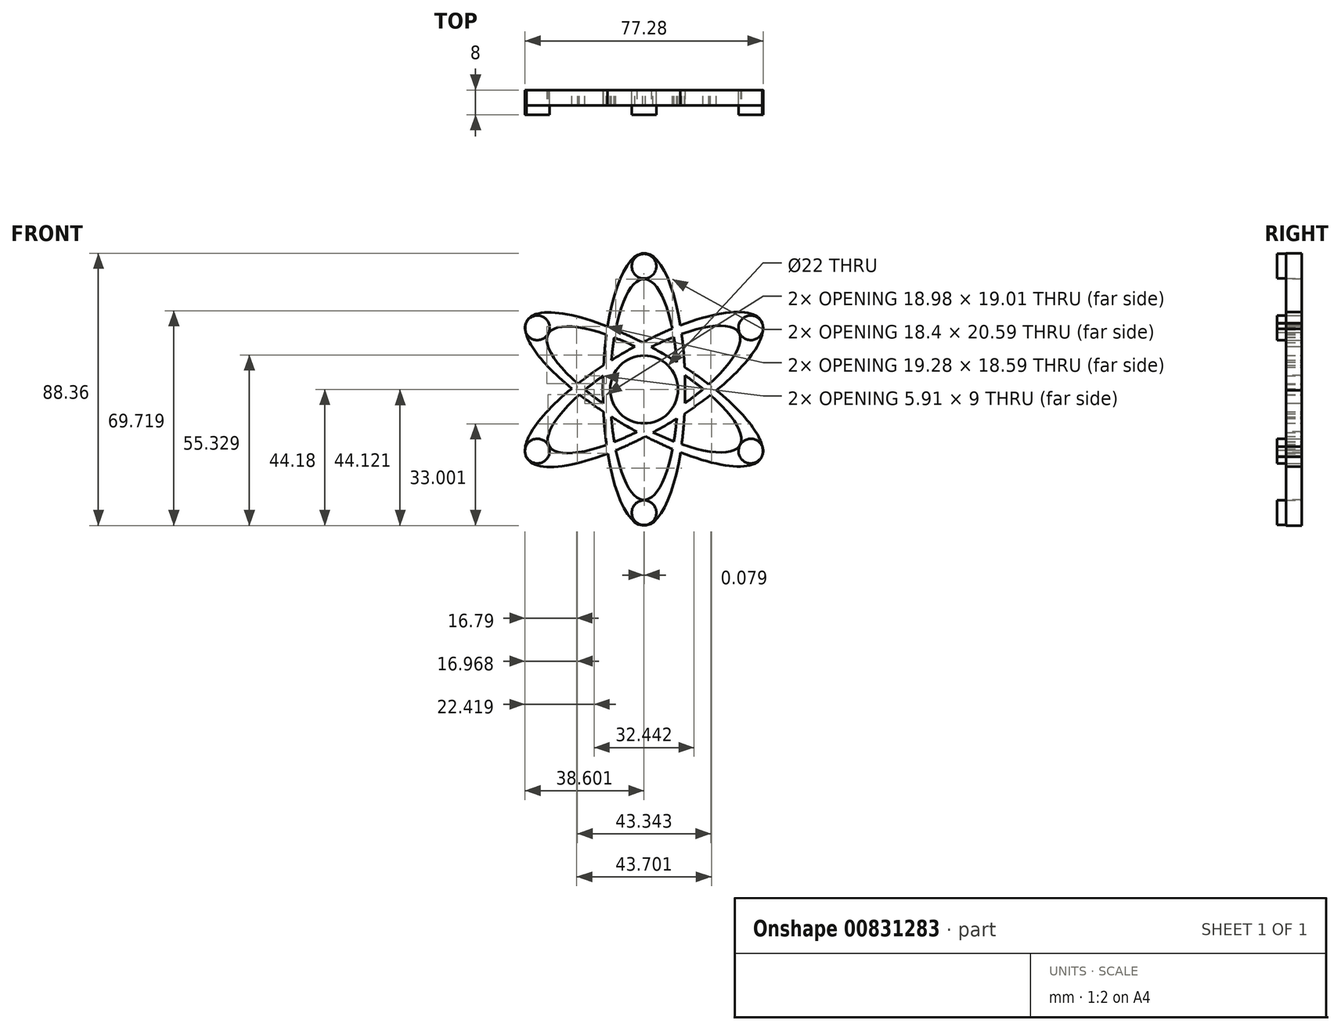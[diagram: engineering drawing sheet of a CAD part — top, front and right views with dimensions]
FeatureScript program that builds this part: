
annotation { "Feature Type Name" : "Feature", "Feature Type Description" : "" }
export const myFeature = defineFeature(function(context is Context, id is Id, definition is map)
    precondition{}
    {
        {
            var Q0;
            Q0=qCreatedBy(makeId("Front.planeOp"),FACE);
            var sketch = newSketch(context, id + "F0", { "sketchPlane" : qUnion([Q0])});
            skCircle(sketch, "E0", {"center": v(0, 0) * mm, "radius": 11 * mm});
            skCircle(sketch, "E1", {"center": v(0, 40) * mm, "radius": 4 * mm});
            skCircle(sketch, "E2", {"center": v(0, -40) * mm, "radius": 4 * mm});
            skEllipticalArc(sketch, "E3", {});
            skEllipticalArc(sketch, "E4", {});
            skCircle(sketch, "E5", {"center": v(34.64, 20) * mm, "radius": 4 * mm});
            skCircle(sketch, "E6", {"center": v(-34.64, -20) * mm, "radius": 4 * mm});
            skEllipticalArc(sketch, "E7", {});
            skEllipticalArc(sketch, "E8", {});
            skCircle(sketch, "E9", {"center": v(-34.64, 20) * mm, "radius": 4 * mm});
            skCircle(sketch, "E10", {"center": v(34.64, -20) * mm, "radius": 4 * mm});
            skEllipticalArc(sketch, "E11", {});
            skEllipticalArc(sketch, "E12", {});
            skEllipticalArc(sketch, "E13.trimOffspring", {});
            skEllipticalArc(sketch, "E14.trimOffspring", {});
            skEllipticalArc(sketch, "E15.trimOffspring", {});
            skEllipticalArc(sketch, "E16.trimOffspring", {});
            skEllipticalArc(sketch, "E17.trimOffspring", {});
            skEllipticalArc(sketch, "E18.trimOffspring", {});
            skEllipticalArc(sketch, "E19.trimOffspring", {});
            skEllipticalArc(sketch, "E20.trimOffspring", {});
            skEllipticalArc(sketch, "E21.trimOffspring", {});
            skEllipticalArc(sketch, "E22.trimOffspring", {});
            skEllipticalArc(sketch, "E23.trimOffspring", {});
            skEllipticalArc(sketch, "E24.trimOffspring", {});
            skEllipticalArc(sketch, "E25.trimOffspring", {});
            skEllipticalArc(sketch, "E26.trimOffspring", {});
            skEllipticalArc(sketch, "E27.trimOffspring", {});
            skEllipticalArc(sketch, "E28.trimOffspring", {});
            skEllipticalArc(sketch, "E29.trimOffspring", {});
            skEllipticalArc(sketch, "E30.trimOffspring", {});
            skEllipticalArc(sketch, "E31.trimOffspring", {});
            skEllipticalArc(sketch, "E32.trimOffspring", {});
            skEllipticalArc(sketch, "E33.trimOffspring", {});
            skEllipticalArc(sketch, "E34.trimOffspring", {});
            skEllipticalArc(sketch, "E35.trimOffspring", {});
            skEllipticalArc(sketch, "E36.trimOffspring", {});
            skEllipticalArc(sketch, "E37.trimOffspring", {});
            skEllipticalArc(sketch, "E38.trimOffspring", {});
            skEllipticalArc(sketch, "E39.trimOffspring", {});
            skEllipticalArc(sketch, "E40.trimOffspring", {});
            skEllipticalArc(sketch, "E41.trimOffspring", {});
            skEllipticalArc(sketch, "E42.trimOffspring", {});
            skEllipticalArc(sketch, "E43.trimOffspring", {});
            skEllipticalArc(sketch, "E44.trimOffspring", {});
            skEllipticalArc(sketch, "E45.trimOffspring", {});
            skEllipticalArc(sketch, "E46.trimOffspring", {});
            skEllipticalArc(sketch, "E47.trimOffspring", {});
            skEllipticalArc(sketch, "E48.trimOffspring", {});
            skEllipticalArc(sketch, "E49.trimOffspring", {});
            skEllipticalArc(sketch, "E50.trimOffspring", {});
            skEllipticalArc(sketch, "E51.trimOffspring", {});
            skEllipticalArc(sketch, "E52.trimOffspring", {});
            skEllipticalArc(sketch, "E53.trimOffspring", {});
            skEllipticalArc(sketch, "E54.trimOffspring", {});
            const initialGuessF0  = {"E3": [0, 0, 0, 1, 0.03583669662475586, 0.010977857535780008, 1.5503457737167272, 1.5912468798730661], "E4": [0, 0, 0, 1, 0.04418346658349037, 0.013337396834647653, 1.4701714838737963, 1.6741165580320305], "E7": [0, 0, -0.8579392037810507, -0.513751226388353, 0.03584875096349461, 0.010985563693539304, 4.969172330873894, 5.191056422950863], "E8": [0, 0, -0.8632553547476697, -0.5047674637885005, 0.04403576959468409, 0.013593075086968625, 4.880502082714586, 5.124257865942808], "E11": [0, 0, -0.8640655163323971, 0.5033793633883178, 0.03598116348014604, 0.010977875538989587, 4.981048986675427, 5.200058194688607], "E12": [0, 0, -0.862123115823514, 0.5066988584581142, 0.04402650923508181, 0.013117720562394524, 4.898530663030038, 5.127888602908416], "E13.trimOffspring": [0, 0, -0.8632553547476697, -0.5047674637885005, 0.04403576959468409, 0.013593075086968625, 4.609604381946106, 4.811440140312948], "E14.trimOffspring": [0, 0, -0.8579392037810507, -0.513751226388353, 0.03584875096349461, 0.010985563693539304, 4.695878637423872, 4.728899323345507], "E15.trimOffspring": [0, 0, 0, 1, 0.03583669662475586, 0.010977857535780008, 4.9627551925164735, 5.2081455373810135], "E16.trimOffspring": [0, 0, -0.8640655163323971, 0.5033793633883178, 0.03598116348014604, 0.010977875538989587, 4.692037264854463, 4.7327406959149165], "E17.trimOffspring": [0, 0, 0, 1, 0.04418346658349037, 0.013337396834647653, 4.877232533582022, 5.131824176420642], "E18.trimOffspring": [0, 0, -0.862123115823514, 0.5066988584581142, 0.04402650923508181, 0.013117720562394524, 4.60611021669764, 4.826068665010817], "E19.trimOffspring": [0, 0, -0.8632553547476697, -0.5047674637885005, 0.04403576959468409, 0.013593075086968625, 1.7389094291247922, 1.9826652123530157], "E20.trimOffspring": [0, 0, 0, 1, 0.04418346658349037, 0.013337396834647653, 4.61176413746359, 4.815709211621823], "E21.trimOffspring": [0, 0, -0.8579392037810507, -0.513751226388353, 0.03584875096349461, 0.010985563693539304, 1.8275796772841009, 2.04946376936107], "E22.trimOffspring": [0, 0, 0, 1, 0.03583669662475586, 0.010977857535780008, 4.6919384273065114, 4.732839533462868], "E23.trimOffspring": [0, 0, -0.8579392037810507, -0.513751226388353, 0.03584875096349461, 0.010985563693539304, 1.554285983834074, 1.5873066697557192], "E24.trimOffspring": [0, 0, -0.8640655163323971, 0.5033793633883178, 0.03598116348014604, 0.010977875538989587, 1.8394563330856333, 2.0584655410988137], "E25.trimOffspring": [0, 0, -0.8632553547476697, -0.5047674637885005, 0.04403576959468409, 0.013593075086968625, 1.4680117283563119, 1.6698474867231567], "E26.trimOffspring": [0, 0, -0.862123115823514, 0.5066988584581142, 0.04402650923508181, 0.013117720562394524, 1.756938009440244, 1.9862959493186234], "E27.trimOffspring": [0, 0, -0.8579392037810507, -0.513751226388353, 0.03584875096349461, 0.010985563693539304, 5.266272148147539, 0.9891609058244074], "E28.trimOffspring": [0, 0, -0.8640655163323971, 0.5033793633883178, 0.03598116348014604, 0.010977875538989587, 1.0940948169627007, 1.3131248907991202], "E29.trimOffspring": [0, 0, -0.8632553547476697, -0.5047674637885005, 0.04403576959468409, 0.013593075086968625, 5.186331359324525, 1.0826333723773631], "E30.trimOffspring": [0, 0, -0.862123115823514, 0.5066988584581142, 0.04402650923508181, 0.013117720562394524, 1.1684900965394949, 1.3957166855960357], "E31.trimOffspring": [0, 0, 0, 1, 0.04418346658349037, 0.013337396834647653, 1.7356398799922295, 1.990231522830849], "E32.trimOffspring": [0, 0, -0.8640655163323971, 0.5033793633883178, 0.03598116348014604, 0.010977875538989587, 1.550444611264671, 1.5911480423251216], "E33.trimOffspring": [0, 0, 0, 1, 0.03583669662475586, 0.010977857535780008, 1.821162538926682, 2.0665528837912204], "E34.trimOffspring": [0, 0, -0.862123115823514, 0.5066988584581142, 0.04402650923508181, 0.013117720562394524, 1.4645175631078486, 1.6844760114210242], "E35.trimOffspring": [0, 0, -0.8640655163323971, 0.5033793633883178, 0.03598116348014604, 0.010977875538989587, 5.285265400945164, 0.9975193424456332], "E36.trimOffspring": [0, 0, 0, 1, 0.04418346658349037, 0.013337396834647653, 1.156424815724134, 1.3921877274411607], "E37.trimOffspring": [0, 0, -0.862123115823514, 0.5066988584581142, 0.04402650923508181, 0.013117720562394524, 5.197762227609222, 1.0897639984535004], "E38.trimOffspring": [0, 0, 0, 1, 0.03583669662475586, 0.010977857535780008, 1.080766215040164, 1.3031144078325463], "E39.trimOffspring": [0, 0, -0.8579392037810507, -0.513751226388353, 0.03584875096349461, 0.010985563693539304, 4.216967542032924, 4.457339788951149], "E40.trimOffspring": [0, 0, 0, 1, 0.04418346658349037, 0.013337396834647653, 5.20225408954963, 1.090604388935838], "E41.trimOffspring": [0, 0, -0.8632553547476697, -0.5047674637885005, 0.04403576959468409, 0.013593075086968625, 4.29438221823192, 4.546569613609151], "E42.trimOffspring": [0, 0, 0, 1, 0.03583669662475586, 0.010977857535780008, 5.295988033251104, 1.0003701535718577], "E43.trimOffspring": [0, 0, -0.8640655163323971, 0.5033793633883178, 0.03598116348014604, 0.010977875538989587, 4.235687470552493, 4.454717544388913], "E44.trimOffspring": [0, 0, -0.8579392037810507, -0.513751226388353, 0.03584875096349461, 0.010985563693539304, 2.1246794945577467, 4.130753559414199], "E45.trimOffspring": [0, 0, -0.862123115823514, 0.5066988584581142, 0.04402650923508181, 0.013117720562394524, 4.310082750129286, 4.537309339185828], "E46.trimOffspring": [0, 0, -0.8632553547476697, -0.5047674637885005, 0.04403576959468409, 0.013593075086968625, 2.044738705734732, 4.224226025967157], "E47.trimOffspring": [0, 0, -0.8640655163323971, 0.5033793633883178, 0.03598116348014604, 0.010977875538989587, 2.1436727473553714, 4.139111996035426], "E48.trimOffspring": [0, 0, 0, 1, 0.04418346658349037, 0.013337396834647653, 4.298017469313926, 4.533780381030953], "E49.trimOffspring": [0, 0, -0.862123115823514, 0.5066988584581142, 0.04402650923508181, 0.013117720562394524, 2.0561695740194295, 4.231356652043294], "E50.trimOffspring": [0, 0, 0, 1, 0.03583669662475586, 0.010977857535780008, 4.222358868629957, 4.44470706142234], "E51.trimOffspring": [0, 0, 0, 1, 0.03583669662475586, 0.010977857535780008, 2.1543953796613105, 4.141962807161651], "E52.trimOffspring": [0, 0, -0.8579392037810507, -0.513751226388353, 0.03584875096349461, 0.010985563693539304, 1.0753748884431307, 1.3157471353613568], "E53.trimOffspring": [0, 0, 0, 1, 0.04418346658349037, 0.013337396834647653, 2.0606614359598368, 4.232197042525632], "E54.trimOffspring": [0, 0, -0.8632553547476697, -0.5047674637885005, 0.04403576959468409, 0.013593075086968625, 1.1527895646421271, 1.4049769600193578]};
            skSetInitialGuess(sketch, initialGuessF0);
            skSolve(sketch);
        }
        {
            var Q0;
            {var subQ0=sQuery(id+"F0.wireOp",EDGE,"E37.trimOffspring");var subQ1=sQuery(id+"F0.wireOp",EDGE,"E9");var subQ2=makeQuery(id+"F0.imprint","INTERSECT",VERTEX,{"disambiguationData":[OD(0.0)],"derivedFrom":[subQ1,subQ0]});Q0=makeQuery(id+"F0.imprint","IMPRINT",FACE,{"disambiguationData":[TD([[makeQuery(id+"F0.imprint","IMPRINT",EDGE,{"disambiguationData":[TD([[subQ2,1.0]])],"derivedFrom":subQ1}),1.0]])]});}
            var Q1;
            Q1=makeQuery(id+"F0.imprint","IMPRINT",FACE,{"disambiguationData":[TD([[makeQuery(id+"F0.imprint","IMPRINT",EDGE,{"derivedFrom":sQuery(id+"F0.wireOp",EDGE,"E1")}),1.0]])]});
            var Q2;
            {var subQ0=sQuery(id+"F0.wireOp",EDGE,"E46.trimOffspring");var subQ1=sQuery(id+"F0.wireOp",EDGE,"E5");var subQ2=makeQuery(id+"F0.imprint","INTERSECT",VERTEX,{"disambiguationData":[OD(0.0)],"derivedFrom":[subQ1,subQ0]});Q2=makeQuery(id+"F0.imprint","IMPRINT",FACE,{"disambiguationData":[TD([[makeQuery(id+"F0.imprint","IMPRINT",EDGE,{"disambiguationData":[TD([[subQ2,1.0]])],"derivedFrom":subQ1}),1.0]])]});}
            var Q3;
            {var subQ0=sQuery(id+"F0.wireOp",EDGE,"E49.trimOffspring");var subQ1=sQuery(id+"F0.wireOp",EDGE,"E10");var subQ2=makeQuery(id+"F0.imprint","INTERSECT",VERTEX,{"disambiguationData":[OD(0.0)],"derivedFrom":[subQ1,subQ0]});Q3=makeQuery(id+"F0.imprint","IMPRINT",FACE,{"disambiguationData":[TD([[makeQuery(id+"F0.imprint","IMPRINT",EDGE,{"disambiguationData":[TD([[subQ2,1.0]])],"derivedFrom":subQ1}),1.0]])]});}
            var Q4;
            Q4=makeQuery(id+"F0.imprint","IMPRINT",FACE,{"disambiguationData":[TD([[makeQuery(id+"F0.imprint","IMPRINT",EDGE,{"derivedFrom":sQuery(id+"F0.wireOp",EDGE,"E2")}),1.0]])]});
            var Q5;
            {var subQ0=sQuery(id+"F0.wireOp",EDGE,"E29.trimOffspring");var subQ1=sQuery(id+"F0.wireOp",EDGE,"E6");var subQ2=makeQuery(id+"F0.imprint","INTERSECT",VERTEX,{"disambiguationData":[OD(0.0)],"derivedFrom":[subQ1,subQ0]});Q5=makeQuery(id+"F0.imprint","IMPRINT",FACE,{"disambiguationData":[TD([[makeQuery(id+"F0.imprint","IMPRINT",EDGE,{"disambiguationData":[TD([[subQ2,1.0]])],"derivedFrom":subQ1}),1.0]])]});}
            extrude(context, id + "F1", {"entities" : qUnion([Q0, Q1, Q2, Q3, Q4, Q5]), "depth" : 8 * mm, "offsetDistance" : 25 * mm});
        }
        {
            var Q0;
            Q0 = qSketchRegion(id + "F0", true);
            extrude(context, id + "F2", {"entities" : qUnion([Q0]), "depth" : 5 * mm, "offsetDistance" : 25 * mm});
        }
    });
